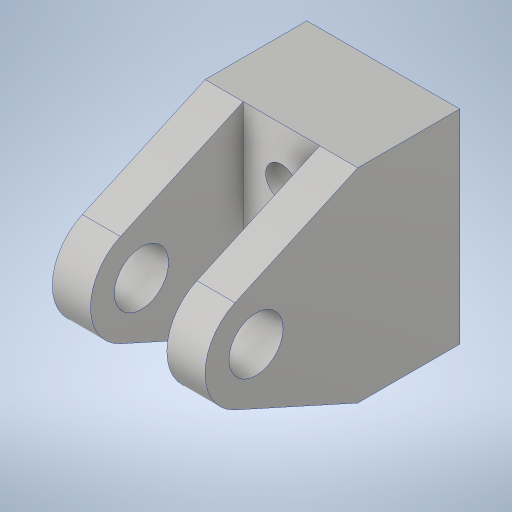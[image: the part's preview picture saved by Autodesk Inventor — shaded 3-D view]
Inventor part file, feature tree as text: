
AUTODESK INVENTOR PART (.ipt)
format: ipt  version: 2023.4 (Build 274418000, 418)  size: 260,608 bytes
history: native  units: in
note: dims shown in document units (in); Inventor stores cm internally (conversion verified against a paired STEP export)
features: sketch x3, projected_geometry x3, extrude x2, hole x2, fillet x1
ambient origin geometry x8: Origin, YZ Plane, XZ Plane, XY Plane, X Axis, Y Axis, Z Axis, Center Point
bodies: Solid1 (feature_tree)
feature tree (11):
  sketch  "Sketch1"  dims[d0=1.0in d1=0.5in]
  extrude  "Extrusion1"  Depth=0.5in
  hole  "Hole1"  [1 undecoded]
  hole  "Hole2"  [1 undecoded]
  extrude  "Extrusion2"  Depth=0.375in
  fillet  "Fillet1"  Radius=0.75in
  sketch  "Sketch2"  dims[d2=0.5in d3=0.5in]
  sketch  "Sketch3"  dims[d4=0.75in d5=0.0in d6=0.266in d7=0.38in d8=0.507in d9=0.25in d10=0.5635in d11=0.536in d12=0.8108in d13=0.5in d14=0.156in d15=0.38in d16=0.375in d17=0.25in d18=0.5635in d19=0.536in d20=0.8108in d21=0.375in d22=0.75in d23=0.0in d24=0.0in d25=0.125in]
  projected_geometry  "Projected Loop1"
  projected_geometry  "Projected Loop2"
  projected_geometry  "Projected Loop3"
note: 2 required parameter values undecoded (feature->parameter linkage not recoverable at this tier; creation-order binding heuristic only, values carry confidence <= 0.55)
